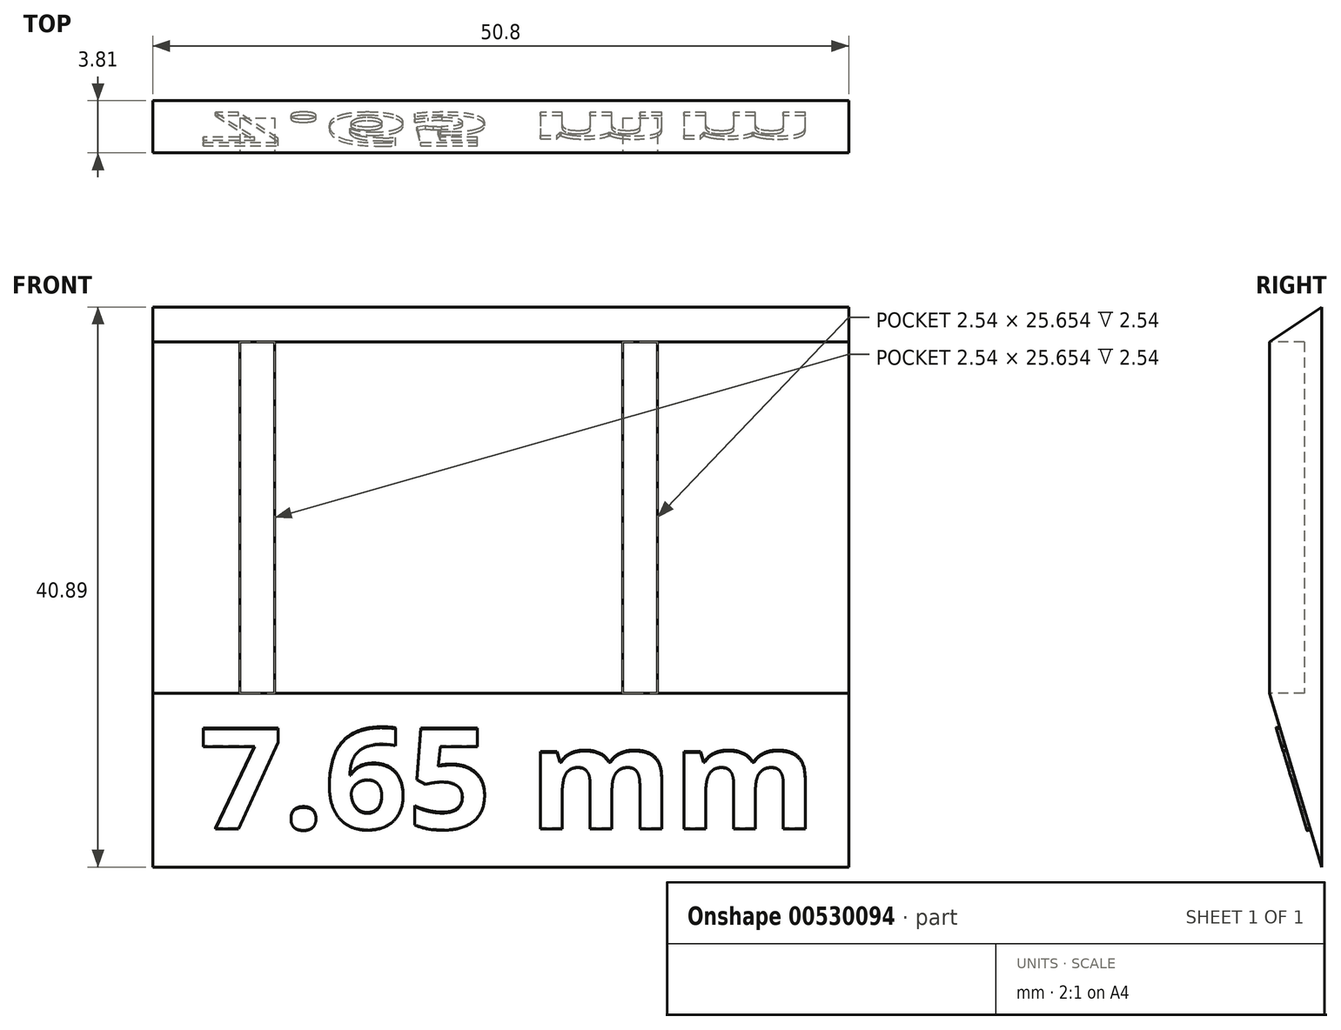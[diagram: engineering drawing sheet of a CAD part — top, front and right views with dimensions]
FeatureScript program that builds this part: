
annotation { "Feature Type Name" : "Feature", "Feature Type Description" : "" }
export const myFeature = defineFeature(function(context is Context, id is Id, definition is map)
    precondition{}
    {
        {
            var Q0;
            Q0=qCreatedBy(makeId("Front.planeOp"),FACE);
            var sketch = newSketch(context, id + "F0", { "sketchPlane" : qUnion([Q0])});
            skLineSegment(sketch, "E0.bottom", {"start": v(-15.88, 10.23) * mm, "end": v(34.92, 10.23) * mm});
            skLineSegment(sketch, "E0.top", {"start": v(-15.88, -15.42) * mm, "end": v(34.92, -15.42) * mm});
            skLineSegment(sketch, "E0.left", {"start": v(-15.88, 10.23) * mm, "end": v(-15.88, -15.42) * mm});
            skLineSegment(sketch, "E0.right", {"start": v(34.92, 10.23) * mm, "end": v(34.92, -15.42) * mm});
            skSolve(sketch);
        }
        {
            var Q0;
            Q0=makeQuery(id+"F0.imprint","IMPRINT",FACE,{"disambiguationData":[TD([[makeQuery(id+"F0.imprint","IMPRINT",EDGE,{"derivedFrom":sQuery(id+"F0.wireOp",EDGE,"E0.bottom")}),-1.0]])]});
            extrude(context, id + "F1", {"entities" : qUnion([Q0]), "depth" : 3.8 * mm, "offsetDistance" : 25.4 * mm});
        }
        {
            var Q0;
            Q0=makeQuery(id+"F1.opExtrude","CAP_FACE",FACE,{"disambiguationData":[OSD([sQuery(id+"F0.wireOp",EDGE,"E0.bottom"),sQuery(id+"F0.wireOp",EDGE,"E0.top"),sQuery(id+"F0.wireOp",EDGE,"E0.left"),sQuery(id+"F0.wireOp",EDGE,"E0.right")])],"isStart":false});
            var sketch = newSketch(context, id + "F2", { "sketchPlane" : qUnion([Q0])});
            skLineSegment(sketch, "E1", {"start": v(-9.53, 10.23) * mm, "end": v(-9.53, -15.42) * mm});
            skLineSegment(sketch, "E2", {"start": v(-6.99, 10.23) * mm, "end": v(-6.99, -15.42) * mm});
            skLineSegment(sketch, "E3", {"start": v(18.41, 10.23) * mm, "end": v(18.41, -15.42) * mm});
            skLineSegment(sketch, "E4", {"start": v(20.95, 10.23) * mm, "end": v(20.95, -15.42) * mm});
            skSolve(sketch);
        }
        {
            var Q0;
            {var subQ0=sQuery(id+"F2.wireOp",EDGE,"E1");Q0=makeQuery(id+"F2.imprint","IMPRINT",FACE,{"disambiguationData":[TD([[makeQuery(id+"F2.imprint","IMPRINT",EDGE,{"derivedFrom":subQ0}),1.0]])]});}
            var Q1;
            {var subQ0=sQuery(id+"F2.wireOp",EDGE,"E3");Q1=makeQuery(id+"F2.imprint","IMPRINT",FACE,{"disambiguationData":[TD([[makeQuery(id+"F2.imprint","IMPRINT",EDGE,{"derivedFrom":subQ0}),1.0]])]});}
            extrude(context, id + "F3", {"entities" : qUnion([Q0, Q1]), "operationType" : NewBodyOperationType.REMOVE, "oppositeDirection" : true, "depth" : 2.54 * mm, "offsetDistance" : 25.4 * mm});
        }
        {
            var Q0;
            Q0=makeQuery(id+"F1.opExtrude","SWEPT_FACE",FACE,{"disambiguationData":[OSD([sQuery(id+"F0.wireOp",EDGE,"E0.left")])]});
            var sketch = newSketch(context, id + "F4", { "sketchPlane" : qUnion([Q0])});
            skLineSegment(sketch, "E5", {"start": v(0, -15.42) * mm, "end": v(0, -28.12) * mm});
            skLineSegment(sketch, "E6", {"start": v(0, -28.12) * mm, "end": v(3.81, -15.42) * mm});
            skLineSegment(sketch, "E7", {"start": v(0, 10.23) * mm, "end": v(0, 12.77) * mm});
            skLineSegment(sketch, "E8", {"start": v(0, 12.77) * mm, "end": v(3.81, 10.23) * mm});
            skSolve(sketch);
        }
        {
            var Q0;
            Q0=makeQuery(id+"F4.imprint","IMPRINT",FACE,{"disambiguationData":[TD([[makeQuery(id+"F4.imprint","IMPRINT",EDGE,{"derivedFrom":sQuery(id+"F4.wireOp",EDGE,"E5")}),1.0]])]});
            var Q1;
            Q1=makeQuery(id+"F4.imprint","IMPRINT",FACE,{"disambiguationData":[TD([[makeQuery(id+"F4.imprint","IMPRINT",EDGE,{"derivedFrom":sQuery(id+"F4.wireOp",EDGE,"E7")}),-1.0]])]});
            extrude(context, id + "F5", {"entities" : qUnion([Q0, Q1]), "operationType" : NewBodyOperationType.ADD, "oppositeDirection" : true, "depth" : 50.8 * mm, "offsetDistance" : 25.4 * mm});
        }
        {
            var Q0;
            Q0=makeQuery(id+"F5.opExtrude","SWEPT_FACE",FACE,{"disambiguationData":[OSD([sQuery(id+"F4.wireOp",EDGE,"E6")])]});
            var sketch = newSketch(context, id + "F6", { "sketchPlane" : qUnion([Q0])});
            skText(sketch, "E9", { "text": "7.65 mm", "fontName": "OpenSans-Bold.ttf"});
            const initialGuessF6  = {"E9": [-0.01249, -0.02395, 1, 0, 0.00768]};
            skSetInitialGuess(sketch, initialGuessF6);
            skSolve(sketch);
        }
        {
            var Q0;
            Q0 = qSketchRegion(id + "F6", true);
            extrude(context, id + "F7", {"entities" : qUnion([Q0]), "operationType" : NewBodyOperationType.ADD, "depth" : 0.25 * mm, "offsetDistance" : 25.4 * mm});
        }
    });
